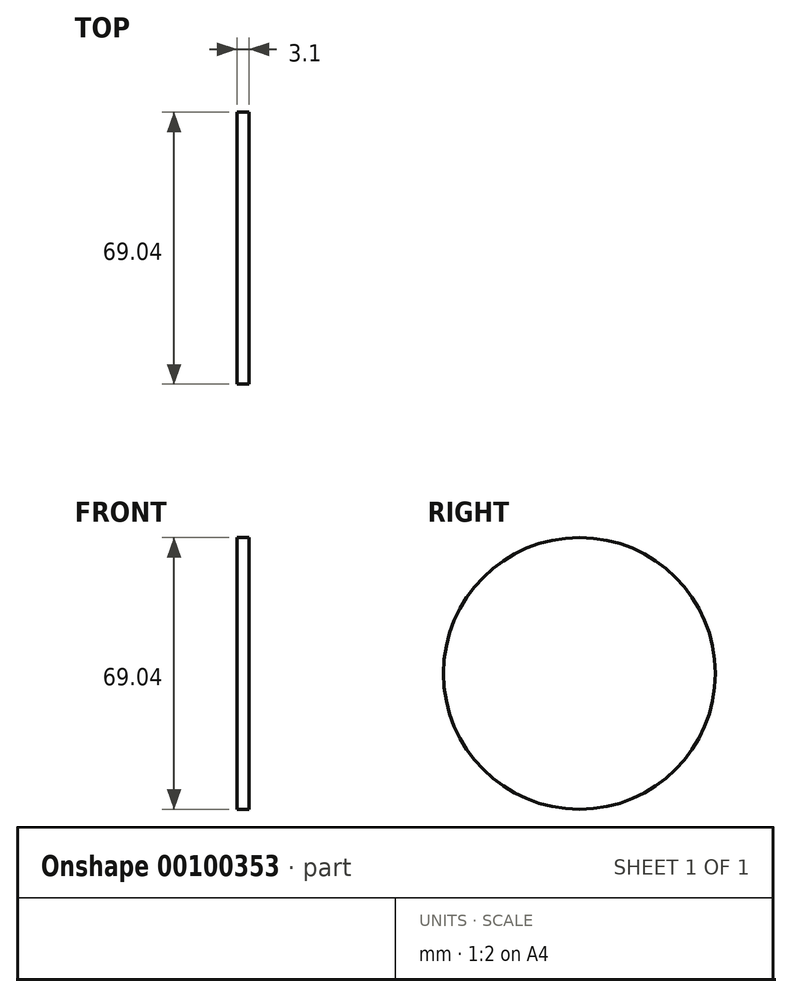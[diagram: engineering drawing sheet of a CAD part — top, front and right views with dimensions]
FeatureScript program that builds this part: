
annotation { "Feature Type Name" : "Feature", "Feature Type Description" : "" }
export const myFeature = defineFeature(function(context is Context, id is Id, definition is map)
    precondition{}
    {
        {
            var Q0;
            Q0=qCreatedBy(makeId("Right.planeOp"),FACE);
            var sketch = newSketch(context, id + "F0", { "sketchPlane" : qUnion([Q0])});
            skCircle(sketch, "E0", {"center": v(0, 0) * mm, "radius": 34.52 * mm});
            skSolve(sketch);
        }
        {
            var Q0;
            Q0=makeQuery(id+"F0.imprint","IMPRINT",FACE,{"disambiguationData":[TD([[makeQuery(id+"F0.imprint","IMPRINT",EDGE,{"derivedFrom":sQuery(id+"F0.wireOp",EDGE,"E0")}),1.0]])]});
            extrude(context, id + "F1", {"entities" : qUnion([Q0]), "depth" : 3.1 * mm});
        }
    });
